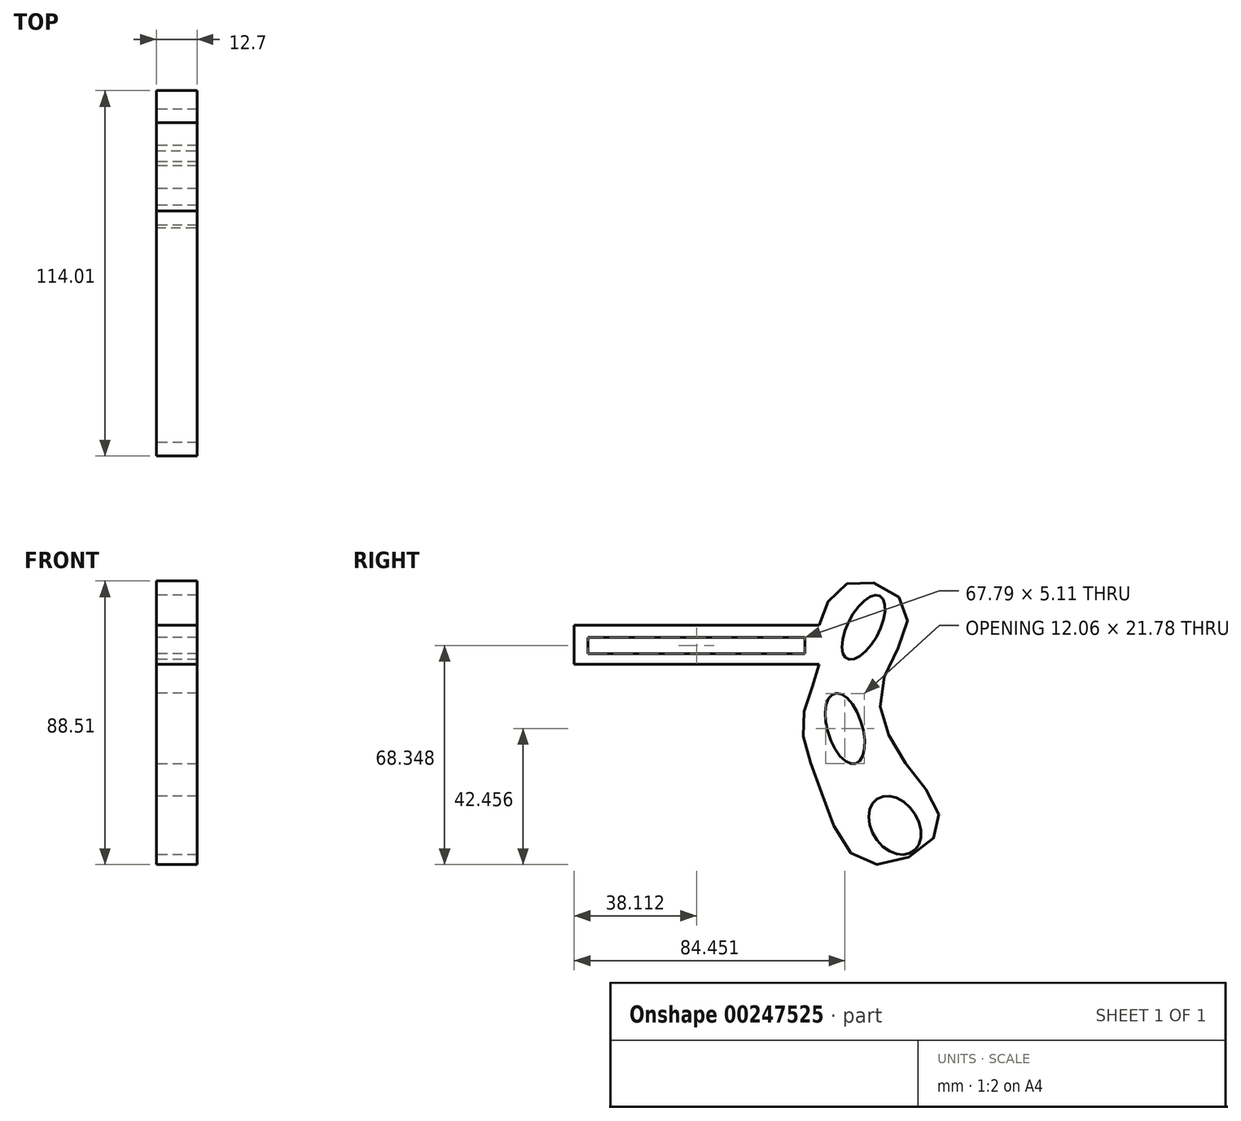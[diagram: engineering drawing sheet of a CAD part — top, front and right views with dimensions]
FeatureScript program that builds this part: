
annotation { "Feature Type Name" : "Feature", "Feature Type Description" : "" }
export const myFeature = defineFeature(function(context is Context, id is Id, definition is map)
    precondition{}
    {
        {
            var Q0;
            Q0=qCreatedBy(makeId("Right.planeOp"),FACE);
            var sketch = newSketch(context, id + "F0", { "sketchPlane" : qUnion([Q0])});
            skLineSegment(sketch, "E0", {"start": v(-76.45, 24.9) * mm, "end": v(0, 24.9) * mm});
            skLineSegment(sketch, "E1", {"start": v(0, 24.9) * mm, "end": v(0, 12.67) * mm});
            skLineSegment(sketch, "E2", {"start": v(0, 12.67) * mm, "end": v(-76.45, 12.67) * mm});
            skLineSegment(sketch, "E3", {"start": v(-76.45, 12.67) * mm, "end": v(-76.45, 24.9) * mm});
            skFitSpline(sketch, "E4", {"points": [v(0, 24.9) * mm, v(10.45, 38.45) * mm, v(27.34, 29.34) * mm, v(19.34, 5.78) * mm, v(27.34, -18.67) * mm, v(37.12, -38.9) * mm, v(15.11, -49.34) * mm, v(0, -25.56) * mm, v(-5.11, -4) * mm, v(0, 12.67) * mm, v(0, 24.9) * mm]});
            skLineSegment(sketch, "E5.bottom", {"start": v(-72.23, 21.11) * mm, "end": v(-4.45, 21.11) * mm});
            skLineSegment(sketch, "E5.top", {"start": v(-72.23, 16) * mm, "end": v(-4.45, 16) * mm});
            skLineSegment(sketch, "E5.left", {"start": v(-72.23, 21.11) * mm, "end": v(-72.23, 16) * mm});
            skLineSegment(sketch, "E5.right", {"start": v(-4.45, 21.11) * mm, "end": v(-4.45, 16) * mm});
            skEllipse(sketch, "E6", {"center": v(13.78, 24.23) * mm, "majorRadius": 11.03 * mm, "minorRadius": 4.95 * mm, "majorAxis": v(0.46, 0.89)});
            skEllipse(sketch, "E7", {"center": v(23.56, -37.56) * mm, "majorRadius": 9.92 * mm, "minorRadius": 7.21 * mm, "majorAxis": v(-0.56, 0.83)});
            skEllipse(sketch, "E8", {"center": v(8, -7.33) * mm, "majorRadius": 11.39 * mm, "minorRadius": 5.43 * mm, "majorAxis": v(0.3, -0.96)});
            skSolve(sketch);
        }
        {
            var Q0;
            Q0 = qSketchRegion(id + "F0", true);
            extrude(context, id + "F1", {"entities" : qUnion([Q0]), "depth" : 12.7 * mm});
        }
    });
